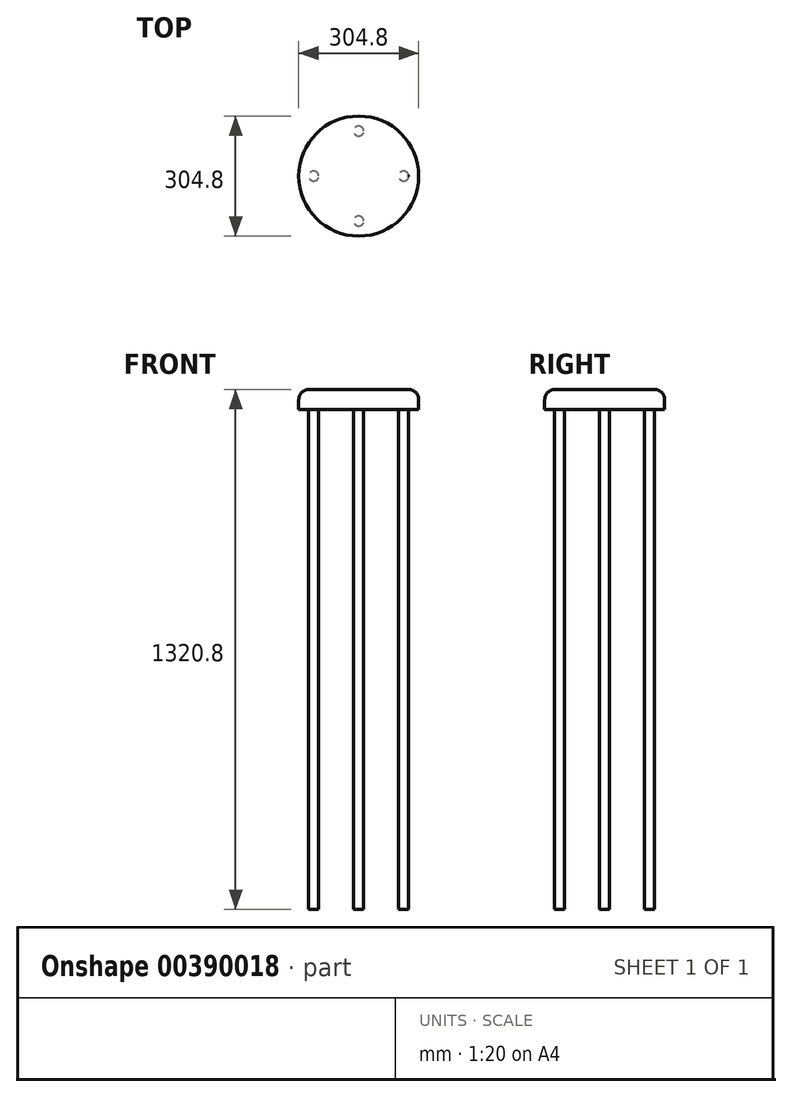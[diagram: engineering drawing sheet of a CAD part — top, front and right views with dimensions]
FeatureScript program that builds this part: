
annotation { "Feature Type Name" : "Feature", "Feature Type Description" : "" }
export const myFeature = defineFeature(function(context is Context, id is Id, definition is map)
    precondition{}
    {
        {
            var Q0;
            Q0=qCreatedBy(makeId("Top.planeOp"),FACE);
            var sketch = newSketch(context, id + "F0", { "sketchPlane" : qUnion([Q0])});
            skCircle(sketch, "E0", {"center": v(0, 0) * mm, "radius": 152.4 * mm});
            skSolve(sketch);
        }
        {
            var Q0;
            Q0 = qSketchRegion(id + "F0", true);
            extrude(context, id + "F1", {"entities" : qUnion([Q0]), "depth" : 50.8 * mm});
        }
        {
            var Q0;
            Q0=makeQuery(id+"F1.opExtrude","CAP_EDGE",EDGE,{"disambiguationData":[OSD([sQuery(id+"F0.wireOp",EDGE,"E0")])],"isStart":false});
            fillet(context, id + "F2", {"entities" : qUnion([Q0]), "radius" : 25.4 * mm, "tangentPropagation" : true, "allowEdgeOverflow" : false});
        }
        {
            var Q0;
            Q0=makeQuery(id+"F1.opExtrude","CAP_FACE",FACE,{"disambiguationData":[OSD([sQuery(id+"F0.wireOp",EDGE,"E0")])],"isStart":true});
            var sketch = newSketch(context, id + "F3", { "sketchPlane" : qUnion([Q0])});
            skCircle(sketch, "E1", {"center": v(0, 114.3) * mm, "radius": 12.7 * mm});
            skSolve(sketch);
        }
        {
            var Q0;
            Q0 = qSketchRegion(id + "F3", true);
            extrude(context, id + "F4", {"entities" : qUnion([Q0]), "depth" : 1270 * mm});
        }
        {
            var Q0;
            Q0=makeQuery(id+"F4.opExtrude","SWEPT_BODY",BODY,{"disambiguationData":[OSD([sQuery(id+"F3.wireOp",EDGE,"E1")])]});
            var Q1;
            Q1=makeQuery(id+"F1.opExtrude","CAP_EDGE",EDGE,{"disambiguationData":[OSD([sQuery(id+"F0.wireOp",EDGE,"E0")])],"isStart":true});
            circularPattern(context, id + "F5", {"entities" : qUnion([Q0]), "axis" : qUnion([Q1]), "angle" : 360 * degree, "instanceCount" : 4, "equalSpace" : true});
        }
    });
